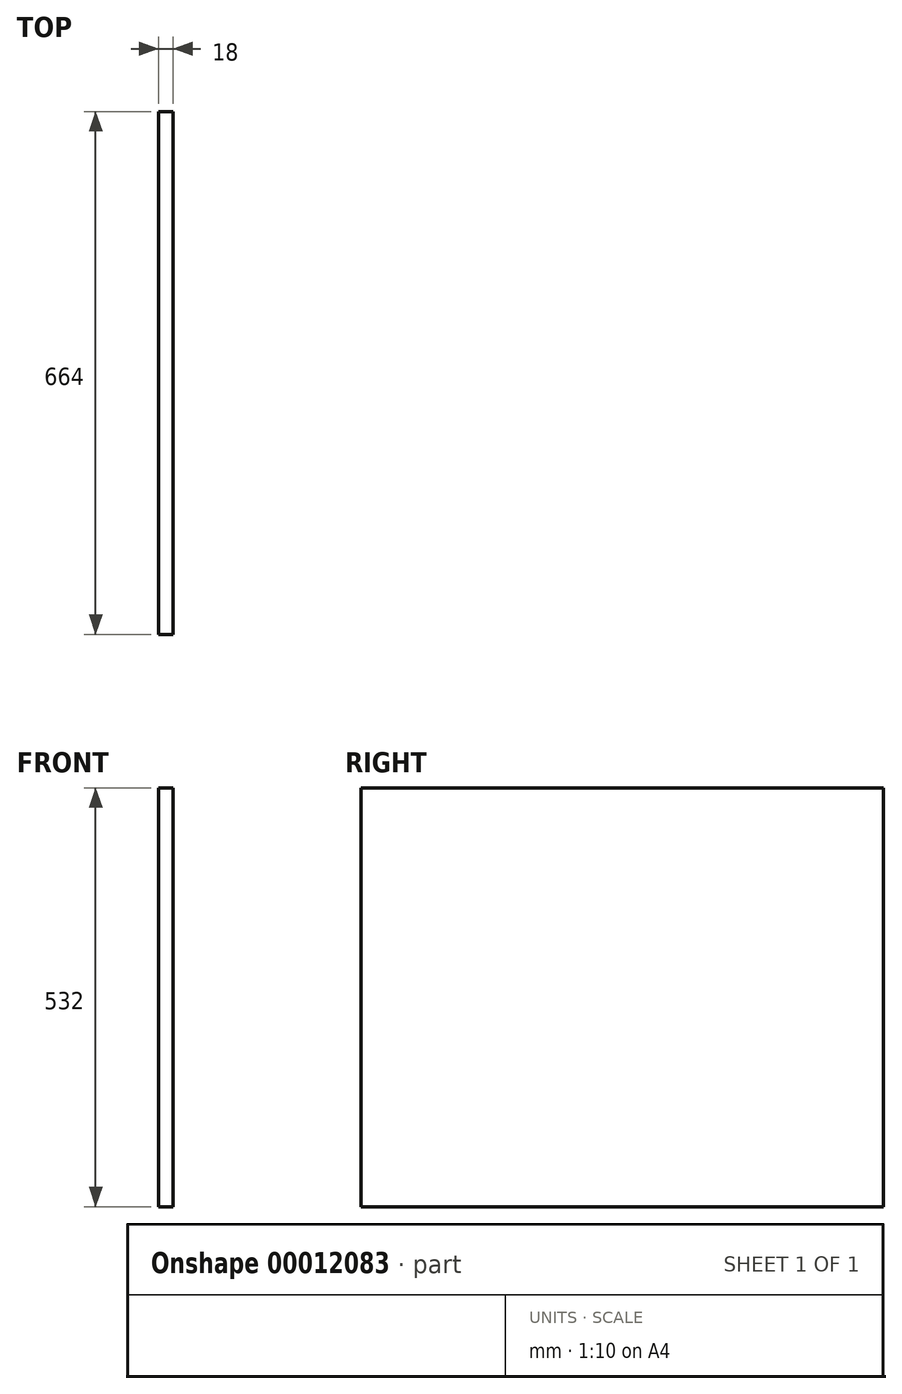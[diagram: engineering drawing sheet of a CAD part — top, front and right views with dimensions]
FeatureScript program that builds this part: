
annotation { "Feature Type Name" : "Feature", "Feature Type Description" : "" }
export const myFeature = defineFeature(function(context is Context, id is Id, definition is map)
    precondition{}
    {
        {
            var Q0;
            Q0=qCreatedBy(makeId("Right.planeOp"),FACE);
            var sketch = newSketch(context, id + "F0", { "sketchPlane" : qUnion([Q0])});
            skLineSegment(sketch, "E0.bottom", {"start": v(0, 0) * mm, "end": v(664, 0) * mm});
            skLineSegment(sketch, "E0.top", {"start": v(0, 532) * mm, "end": v(664, 532) * mm});
            skLineSegment(sketch, "E0.left", {"start": v(0, 0) * mm, "end": v(0, 532) * mm});
            skLineSegment(sketch, "E0.right", {"start": v(664, 0) * mm, "end": v(664, 532) * mm});
            skSolve(sketch);
        }
        {
            var Q0;
            Q0 = qSketchRegion(id + "F0", true);
            extrude(context, id + "F1", {"entities" : qUnion([Q0]), "depth" : 18 * mm});
        }
    });
